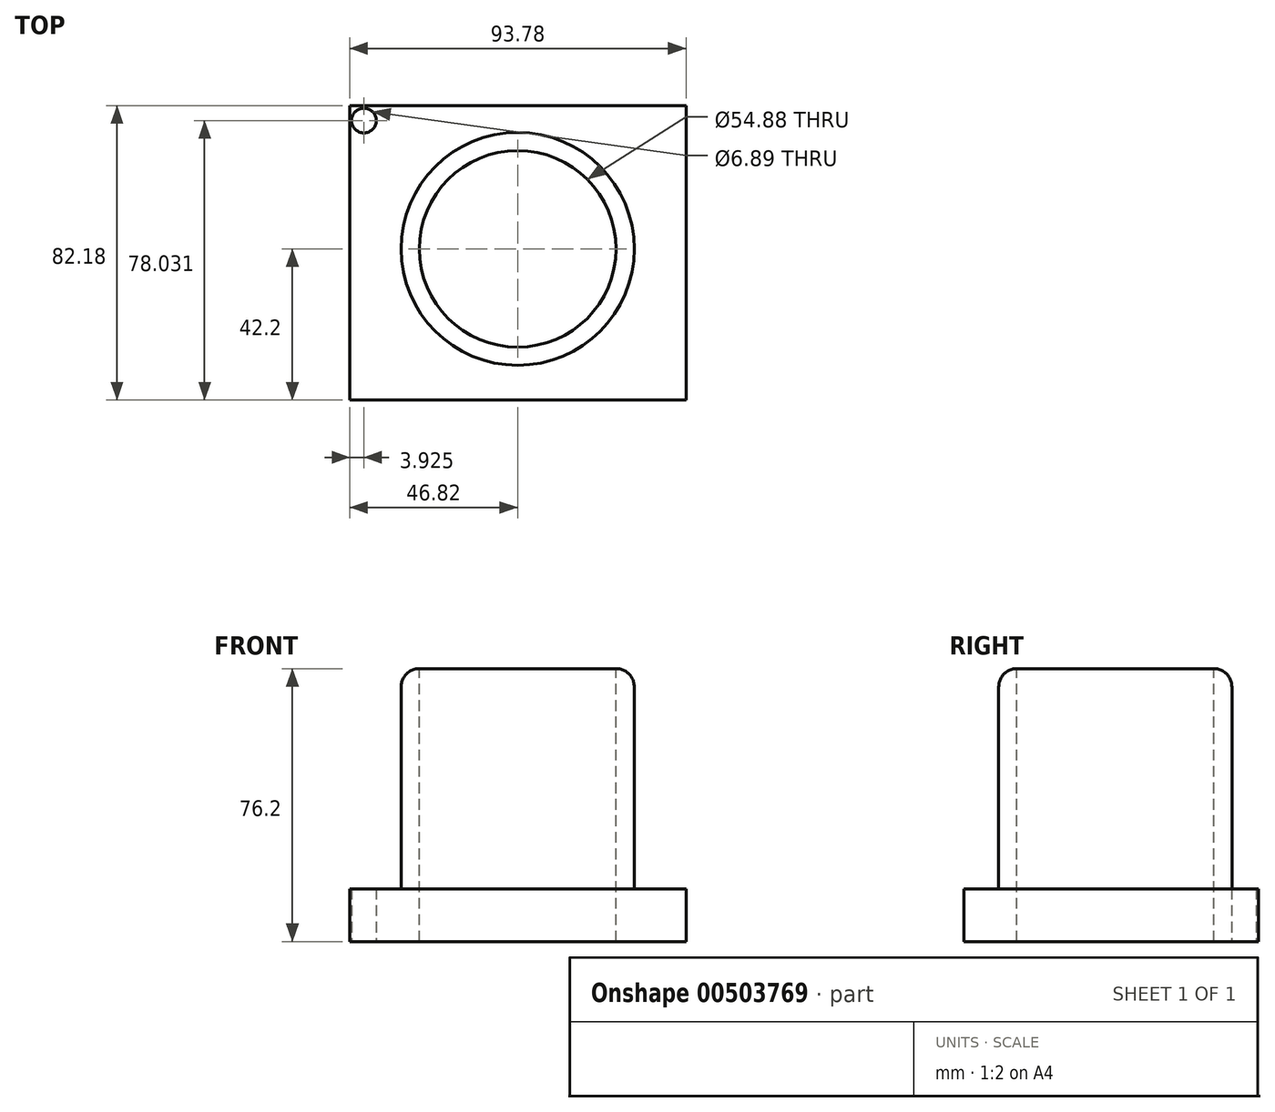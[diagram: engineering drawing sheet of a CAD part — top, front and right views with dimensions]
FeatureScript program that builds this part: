
annotation { "Feature Type Name" : "Feature", "Feature Type Description" : "" }
export const myFeature = defineFeature(function(context is Context, id is Id, definition is map)
    precondition{}
    {
        {
            var Q0;
            Q0=qCreatedBy(makeId("Top.planeOp"),FACE);
            var sketch = newSketch(context, id + "F0", { "sketchPlane" : qUnion([Q0])});
            skCircle(sketch, "E0", {"center": v(0, 0) * mm, "radius": 32.52 * mm});
            skSolve(sketch);
        }
        {
            var Q0;
            Q0=makeQuery(id+"F0.imprint","IMPRINT",FACE,{"disambiguationData":[TD([[makeQuery(id+"F0.imprint","IMPRINT",EDGE,{"derivedFrom":sQuery(id+"F0.wireOp",EDGE,"E0")}),1.0]])]});
            extrude(context, id + "F1", {"entities" : qUnion([Q0]), "depth" : 76.2 * mm});
        }
        {
            var Q0;
            Q0=makeQuery(id+"F1.opExtrude","CAP_EDGE",EDGE,{"disambiguationData":[OSD([sQuery(id+"F0.wireOp",EDGE,"E0")])],"isStart":false});
            fillet(context, id + "F2", {"entities" : qUnion([Q0]), "radius" : 5.08 * mm, "tangentPropagation" : true, "allowEdgeOverflow" : false});
        }
        {
            var Q0;
            Q0=makeQuery(id+"F1.opExtrude","CAP_FACE",FACE,{"disambiguationData":[OSD([sQuery(id+"F0.wireOp",EDGE,"E0")])],"isStart":false});
            extrude(context, id + "F3", {"entities" : qUnion([Q0]), "operationType" : NewBodyOperationType.REMOVE, "oppositeDirection" : true, "depth" : 124.7 * mm});
        }
        {
            var Q0;
            Q0=makeQuery(id+"F1.opExtrude","CAP_EDGE",EDGE,{"disambiguationData":[OSD([sQuery(id+"F0.wireOp",EDGE,"E0")])],"isStart":true});
            fillet(context, id + "F4", {"entities" : qUnion([Q0]), "radius" : 5.08 * mm, "tangentPropagation" : true, "allowEdgeOverflow" : false});
        }
        {
            var Q0;
            Q0=qCreatedBy(makeId("Top.planeOp"),FACE);
            var sketch = newSketch(context, id + "F5", { "sketchPlane" : qUnion([Q0])});
            skLineSegment(sketch, "E1.bottom", {"start": v(-46.82, -42.2) * mm, "end": v(46.96, -42.2) * mm});
            skLineSegment(sketch, "E1.top", {"start": v(-46.82, 39.98) * mm, "end": v(46.96, 39.98) * mm});
            skLineSegment(sketch, "E1.left", {"start": v(-46.82, -42.2) * mm, "end": v(-46.82, 39.98) * mm});
            skLineSegment(sketch, "E1.right", {"start": v(46.96, -42.2) * mm, "end": v(46.96, 39.98) * mm});
            skSolve(sketch);
        }
        {
            var Q0;
            Q0=makeQuery(id+"F5.imprint","IMPRINT",FACE,{"disambiguationData":[TD([[makeQuery(id+"F5.imprint","IMPRINT",EDGE,{"derivedFrom":sQuery(id+"F5.wireOp",EDGE,"E1.bottom")}),1.0]])]});
            extrude(context, id + "F6", {"entities" : qUnion([Q0]), "operationType" : NewBodyOperationType.ADD, "depth" : 14.73 * mm});
        }
        {
            var Q0;
            Q0=makeQuery(id+"F6.boolean.opBoolean","SPLIT",FACE,{"disambiguationData":[TD([makeQuery(id+"F3.boolean.opBoolean","COPY",FACE,{"derivedFrom":makeQuery(id+"F3.opExtrude","SWEPT_FACE",FACE,{"disambiguationData":[OSD([sQuery(id+"F0.wireOp",EDGE,"E0")])]})})])],"derivedFrom":makeQuery(id+"F6.opExtrude","CAP_FACE",FACE,{"disambiguationData":[OSD([sQuery(id+"F5.wireOp",EDGE,"E1.bottom"),sQuery(id+"F5.wireOp",EDGE,"E1.top"),sQuery(id+"F5.wireOp",EDGE,"E1.left"),sQuery(id+"F5.wireOp",EDGE,"E1.right")])],"isStart":false})});
            extrude(context, id + "F7", {"entities" : qUnion([Q0]), "operationType" : NewBodyOperationType.REMOVE, "oppositeDirection" : true, "depth" : 36.83 * mm});
        }
        {
            var Q0;
            Q0=qCreatedBy(makeId("Top.planeOp"),FACE);
            var sketch = newSketch(context, id + "F8", { "sketchPlane" : qUnion([Q0])});
            skCircle(sketch, "E2", {"center": v(-42.9, 35.83) * mm, "radius": 3.45 * mm});
            skSolve(sketch);
        }
        {
            var Q0;
            Q0=makeQuery(id+"F8.imprint","IMPRINT",FACE,{"disambiguationData":[TD([[makeQuery(id+"F8.imprint","IMPRINT",EDGE,{"derivedFrom":sQuery(id+"F8.wireOp",EDGE,"E2")}),1.0]])]});
            var Q1;
            Q1=sQuery(id+"F8.wireOp",EDGE,"E2");
            extrude(context, id + "F9", {"entities" : qUnion([Q0]), "operationType" : NewBodyOperationType.REMOVE, "surfaceEntities" : qUnion([Q1]), "depth" : 19.56 * mm, "offsetDistance" : 25.4 * mm});
        }
    });
